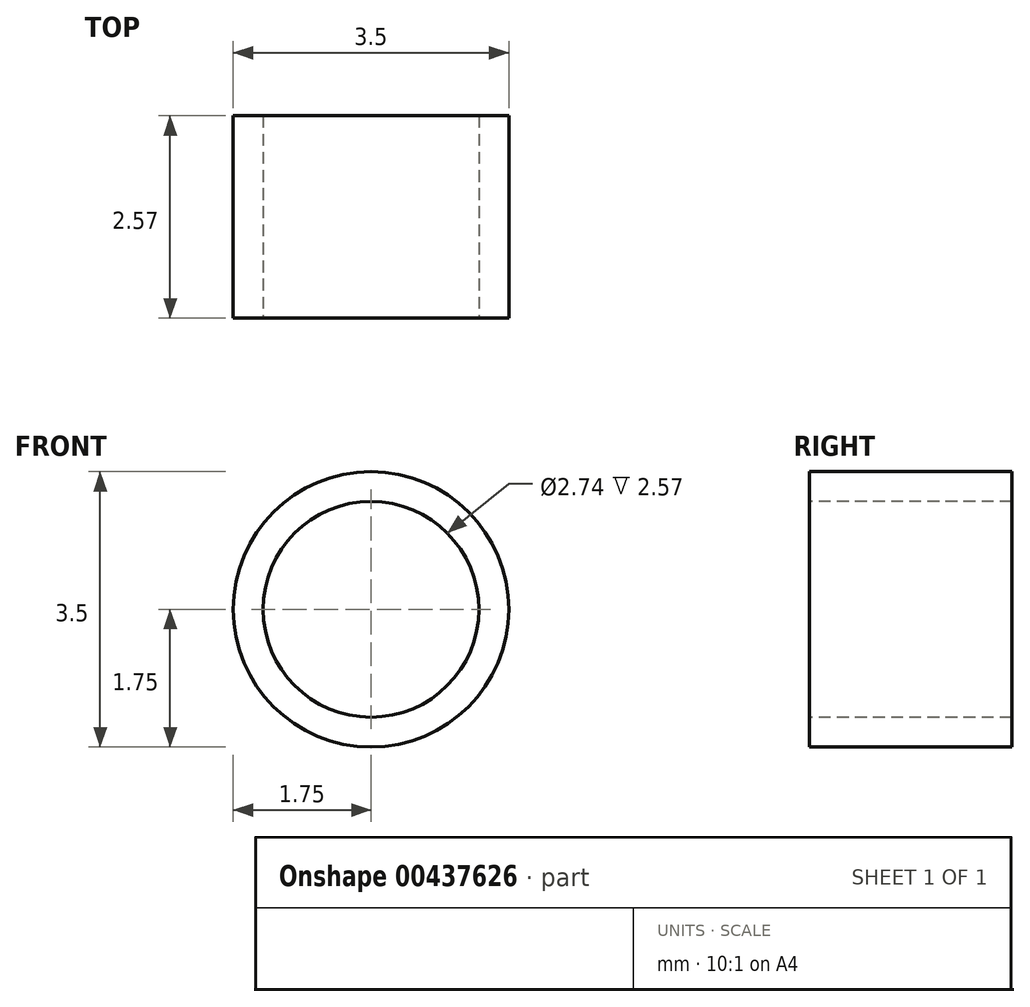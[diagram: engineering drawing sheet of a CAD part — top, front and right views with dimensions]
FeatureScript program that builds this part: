
annotation { "Feature Type Name" : "Feature", "Feature Type Description" : "" }
export const myFeature = defineFeature(function(context is Context, id is Id, definition is map)
    precondition{}
    {
        {
            var Q0;
            Q0=qCreatedBy(makeId("Front.planeOp"),FACE);
            var sketch = newSketch(context, id + "F0", { "sketchPlane" : qUnion([Q0])});
            skCircle(sketch, "E0", {"center": v(0, 0) * mm, "radius": 1.75 * mm});
            skCircle(sketch, "E1", {"center": v(0, 0) * mm, "radius": 1.37 * mm});
            skSolve(sketch);
        }
        {
            var Q0;
            Q0 = qSketchRegion(id + "F0", true);
            extrude(context, id + "F1", {"entities" : qUnion([Q0]), "oppositeDirection" : true, "depth" : 2.57 * mm});
        }
    });
